# Revit family: FU_Chair_Sandler_Myra 2.5
name_source: partatom
category: Furniture
units: mm (PartAtom-declared; Revit-internal decimal feet)

## family parameters
Always vertical = Yes
Cut with Voids When Loaded = No
OmniClass Number = 23.40.20.00
OmniClass Title = General Furniture and Specialties
Room Calculation Point = No
Shared = No
Work Plane-Based = No

## types (1)
- Myra 2.5
    Default Elevation = 0 mm  [stored 0 ft]
    Depth = 740 mm  [stored 2.42782 ft]
    Description = Swivel armchair with a fully upholstered seat and back on a steel 4-leg frame. The frame has a 180° swivel mechanism with memory return. With contrast stitching in red or rope color.
    Frame = Sandler - Frame - Polished Aluminium
    Height = 890 mm  [stored 2.91995 ft]
    Manufacturer = Sandler
    Model = Myra 2.5
    Seat = Fabric - Mainline Flax - Pimlico MLF34
    URL = https://www.sandlerseating.com
    Width = 810 mm

note: [stored X ft] marks values corroborated as IEEE doubles in the binary element streams (Revit-internal decimal feet)

## geometry (parser evidence)
native form markers: Sweep x5
no freeform markers — native parametric forms only
